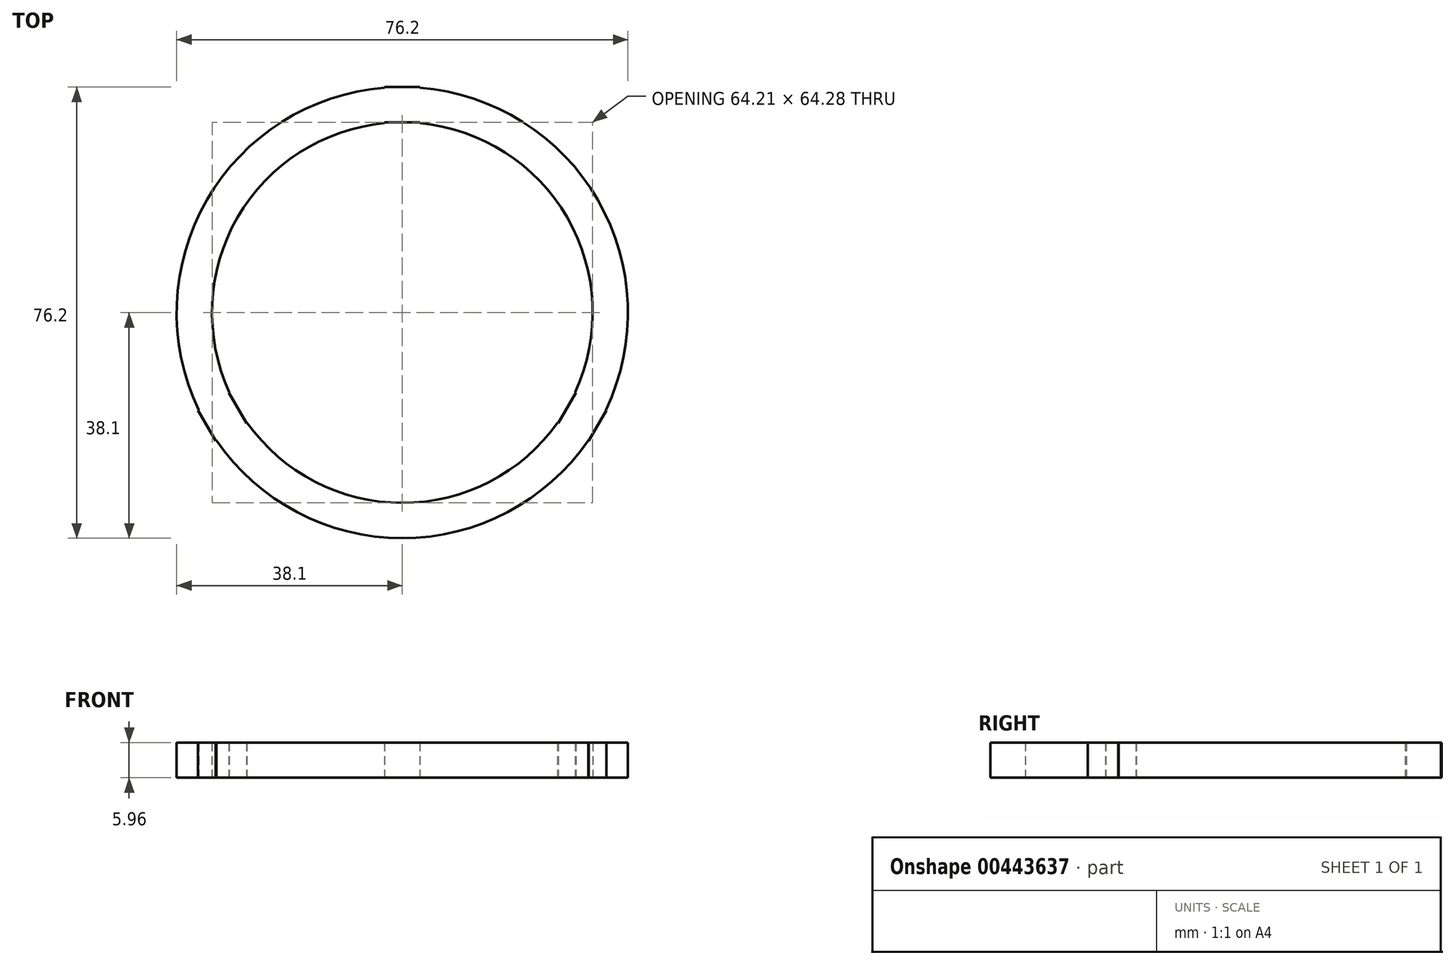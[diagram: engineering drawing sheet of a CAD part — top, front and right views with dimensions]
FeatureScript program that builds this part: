
annotation { "Feature Type Name" : "Feature", "Feature Type Description" : "" }
export const myFeature = defineFeature(function(context is Context, id is Id, definition is map)
    precondition{}
    {
        {
            var Q0;
            Q0=qCreatedBy(makeId("Top.planeOp"),FACE);
            var sketch = newSketch(context, id + "F0", { "sketchPlane" : qUnion([Q0])});
            skCircle(sketch, "E0", {"center": v(0, 0) * mm, "radius": 38.1 * mm});
            skCircle(sketch, "E1", {"center": v(0, 0) * mm, "radius": 32.14 * mm});
            skCircle(sketch, "E2.cCircle", {"center": v(0, 0) * mm, "radius": 38.1 * mm, "construction": true});
            skLineSegment(sketch, "E3", {"start": v(0, 0) * mm, "end": v(0, 32.14) * mm});
            skLineSegment(sketch, "E4", {"start": v(0, 0) * mm, "end": v(-27.83, -16.07) * mm});
            skLineSegment(sketch, "E5", {"start": v(0, 0) * mm, "end": v(27.83, -16.07) * mm});
            skLineSegment(sketch, "E6", {"start": v(0, 32.14) * mm, "end": v(0, 38.1) * mm});
            skLineSegment(sketch, "E7", {"start": v(-27.83, -16.07) * mm, "end": v(-33, -19.05) * mm});
            skLineSegment(sketch, "E8", {"start": v(27.83, -16.07) * mm, "end": v(33, -19.05) * mm});
            skPoint(sketch, "E9", {"position": v(0, 35.12) * mm});
            skPoint(sketch, "E10", {"position": v(-30.41, -17.56) * mm});
            skPoint(sketch, "E11", {"position": v(30.41, -17.56) * mm});
            skLineSegment(sketch, "E12.bottom", {"start": v(2.98, 38.1) * mm, "end": v(-2.98, 38.1) * mm});
            skLineSegment(sketch, "E12.top", {"start": v(2.98, 32.14) * mm, "end": v(-2.98, 32.14) * mm});
            skLineSegment(sketch, "E12.left", {"start": v(2.98, 38.1) * mm, "end": v(2.98, 32.14) * mm});
            skLineSegment(sketch, "E12.right", {"start": v(-2.98, 38.1) * mm, "end": v(-2.98, 32.14) * mm});
            skLineSegment(sketch, "E13", {"start": v(-2.98, 32.14) * mm, "end": v(-2.98, 32) * mm});
            skLineSegment(sketch, "E14", {"start": v(2.98, 32.14) * mm, "end": v(2.98, 32) * mm});
            skLineSegment(sketch, "E15.bottom", {"start": v(-34.49, -16.47) * mm, "end": v(-29.32, -13.49) * mm});
            skLineSegment(sketch, "E15.top", {"start": v(-31.5, -21.63) * mm, "end": v(-26.34, -18.65) * mm});
            skLineSegment(sketch, "E15.left", {"start": v(-34.49, -16.47) * mm, "end": v(-31.5, -21.63) * mm});
            skLineSegment(sketch, "E15.right", {"start": v(-29.32, -13.49) * mm, "end": v(-26.34, -18.65) * mm});
            skLineSegment(sketch, "E16", {"start": v(-26.34, -18.65) * mm, "end": v(-26.22, -18.58) * mm});
            skLineSegment(sketch, "E17", {"start": v(-29.32, -13.49) * mm, "end": v(-29.2, -13.42) * mm});
            skLineSegment(sketch, "E18.bottom", {"start": v(34.49, -16.47) * mm, "end": v(29.32, -13.49) * mm});
            skLineSegment(sketch, "E18.top", {"start": v(31.5, -21.63) * mm, "end": v(26.34, -18.65) * mm});
            skLineSegment(sketch, "E18.left", {"start": v(34.49, -16.47) * mm, "end": v(31.5, -21.63) * mm});
            skLineSegment(sketch, "E18.right", {"start": v(29.32, -13.49) * mm, "end": v(26.34, -18.65) * mm});
            skLineSegment(sketch, "E19", {"start": v(26.34, -18.65) * mm, "end": v(26.22, -18.58) * mm});
            skLineSegment(sketch, "E20", {"start": v(29.32, -13.49) * mm, "end": v(29.2, -13.42) * mm});
            skSolve(sketch);
        }
        {
            var Q0;
            Q0 = qSketchRegion(id + "F0", true);
            extrude(context, id + "F1", {"entities" : qUnion([Q0]), "depth" : 5.96 * mm});
        }
    });
